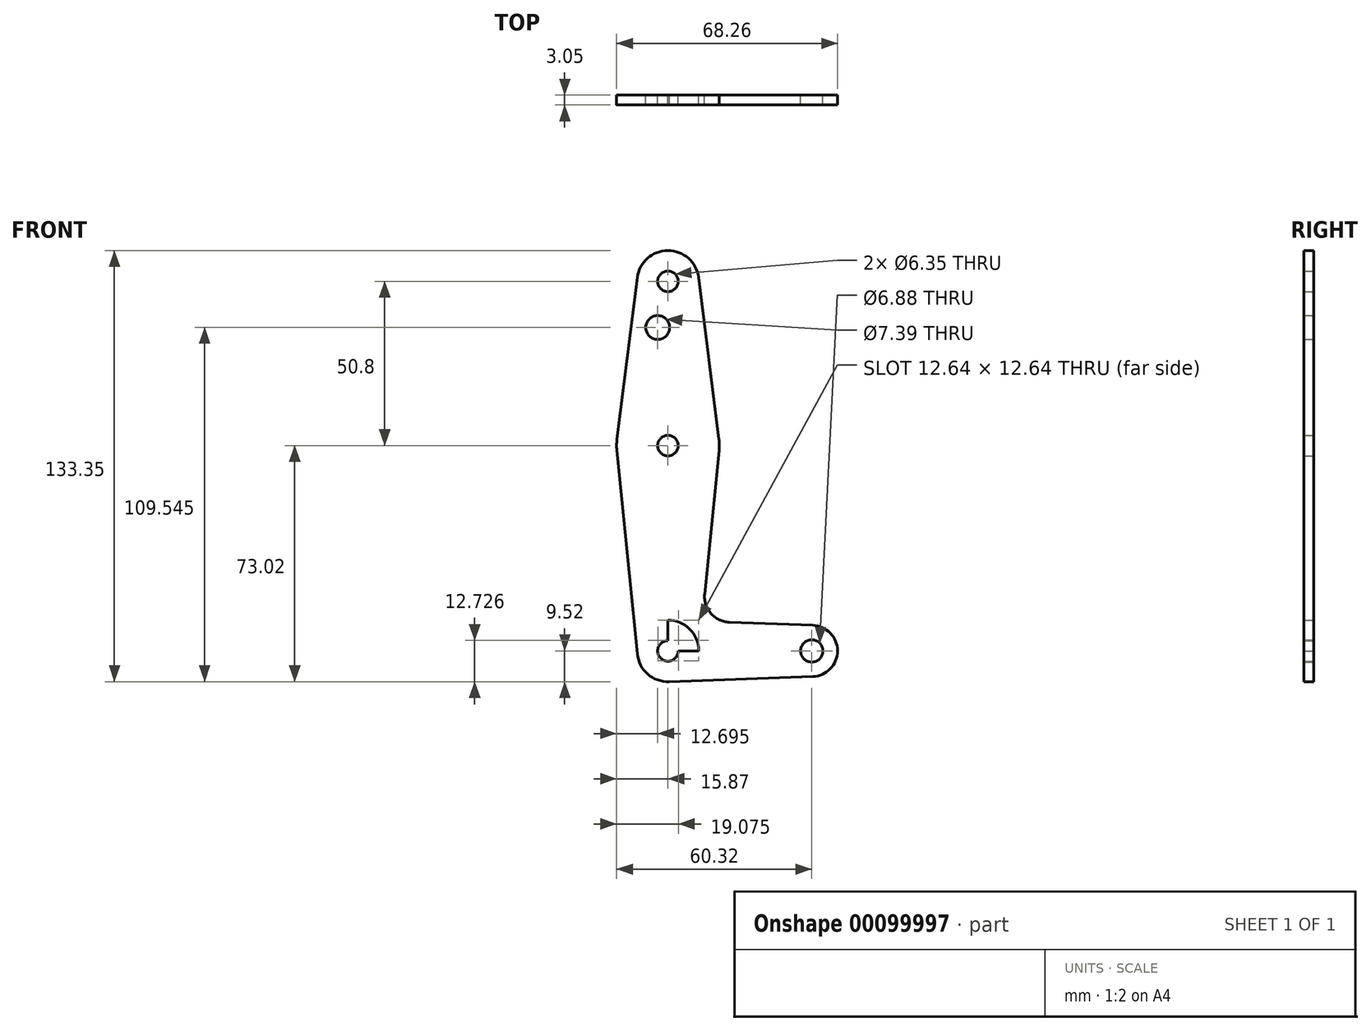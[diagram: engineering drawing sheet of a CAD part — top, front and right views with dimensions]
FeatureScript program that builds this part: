
annotation { "Feature Type Name" : "Feature", "Feature Type Description" : "" }
export const myFeature = defineFeature(function(context is Context, id is Id, definition is map)
    precondition{}
    {
        {
            var Q0;
            Q0=qCreatedBy(makeId("Front.planeOp"),FACE);
            var sketch = newSketch(context, id + "F0", { "sketchPlane" : qUnion([Q0])});
            skLineSegment(sketch, "E0", {"start": v(0, 0) * mm, "end": v(0, 63.5) * mm});
            skLineSegment(sketch, "E1", {"start": v(0, 63.5) * mm, "end": v(0, 114.3) * mm});
            skCircle(sketch, "E2", {"center": v(0, 63.5) * mm, "radius": 15.88 * mm});
            skCircle(sketch, "E3", {"center": v(0, 114.3) * mm, "radius": 9.53 * mm});
            skCircle(sketch, "E4", {"center": v(0, 0) * mm, "radius": 9.53 * mm});
            skLineSegment(sketch, "E5", {"start": v(0, 0) * mm, "end": v(44.45, 0) * mm});
            skCircle(sketch, "E6", {"center": v(44.45, 0) * mm, "radius": 7.94 * mm});
            skLineSegment(sketch, "E7", {"start": v(-9.45, 115.5) * mm, "end": v(-15.75, 65.48) * mm});
            skLineSegment(sketch, "E8", {"start": v(9.45, 115.5) * mm, "end": v(15.75, 65.48) * mm});
            skLineSegment(sketch, "E9", {"start": v(-15.8, 61.91) * mm, "end": v(-9.48, -0.95) * mm});
            skLineSegment(sketch, "E10", {"start": v(15.8, 61.91) * mm, "end": v(11.34, 17.6) * mm});
            skLineSegment(sketch, "E11", {"start": v(44.73, 7.93) * mm, "end": v(18.97, 8.85) * mm});
            skLineSegment(sketch, "E12", {"start": v(44.73, -7.93) * mm, "end": v(0.34, -9.52) * mm});
            skCircle(sketch, "E13", {"center": v(0, 114.3) * mm, "radius": 3.18 * mm});
            skCircle(sketch, "E14", {"center": v(0, 63.5) * mm, "radius": 3.18 * mm});
            skCircle(sketch, "E15", {"center": v(0, 0) * mm, "radius": 3.18 * mm});
            skCircle(sketch, "E16", {"center": v(44.45, 0) * mm, "radius": 3.44 * mm});
            skCircle(sketch, "E17", {"center": v(-3.18, 100.03) * mm, "radius": 3.7 * mm});
            skArc(sketch, "E18.filletArc", {"start": v(11.34, 17.6) * mm, "mid": v(13.26, 11.57) * mm, "end": v(18.97, 8.85) * mm});
            skSolve(sketch);
        }
        {
            var Q0;
            Q0 = qSketchRegion(id + "F0", true);
            extrude(context, id + "F1", {"entities" : qUnion([Q0]), "depth" : 3.05 * mm});
        }
    });
